# Revit family: LED LANDSCAPE 05_LKG0536WW.13
name_source: partatom
category: Luminarias
units: mm (PartAtom-declared; Revit-internal decimal feet)

## family parameters
Compartido = No
Corte con vacíos al cargar = No
Cota de conector redondo = Diámetro de uso
Origen de luz = Sí
Punto de cálculo de habitación = No
Se basa en plano de trabajo = Sí
Siempre vertical = No
Tipo de pieza = Normal

## types (1)
- LED LANDSCAPE 05_LKG0536WW.13
    Cambio de temperatura de color de luz atenuada = <Ninguno>
    Comentarios de vataje = 100-277V
    Descripción = LUMINARIA DE JARDIN CON ESTACA, CUERPO DE ALUMINIO FUNDIDO A PRESION CUBIERTO CON POLVO GRIS OSCURO Y VIDRIO TEMPLADO DE 4MM CON UN PESO DE 1.8KG, USO PARA INTERIORES Y EXTERIORES IP 66, IK 05, 5 LED TIPO OSRAM CON UNA POTENCIA DE 9.5W, IRC 80, 586 LUMENES, TEMPERATURA EN BLANCO CALIDO 3000K, EFICIENCIA DE 57.45 LM/W, APERTURA DE 13 GRADOS POR PROYECTO, DIMMEABLE OPCIONAL EN TRIAC, CABLE DE 2.0M H05RN-F, CORRIENTE DE OPERACIÓN 80mA, ALIMENTADO A 100-277V.
    Elevación por defecto = 0 mm  [stored 0 ft]
    Fabricante = BRILLANT
    Filtro de color = 16777215
    Longitud de símbolo de origen de luz = 500 mm  [stored 1.64042 ft]
    Lámpara = OSRAM
    Modelo = LKG0536WW.13
    Watt per fixture = 9.5
    Ángulo de campo de foco = 13.00°
    Ángulo de enfoque = 13.00°
    Ángulo de inclinación = 60.00°

note: [stored X ft] marks values corroborated as IEEE doubles in the binary element streams (Revit-internal decimal feet)

## geometry (parser evidence)
native form markers: Blend x2
no freeform markers — native parametric forms only
